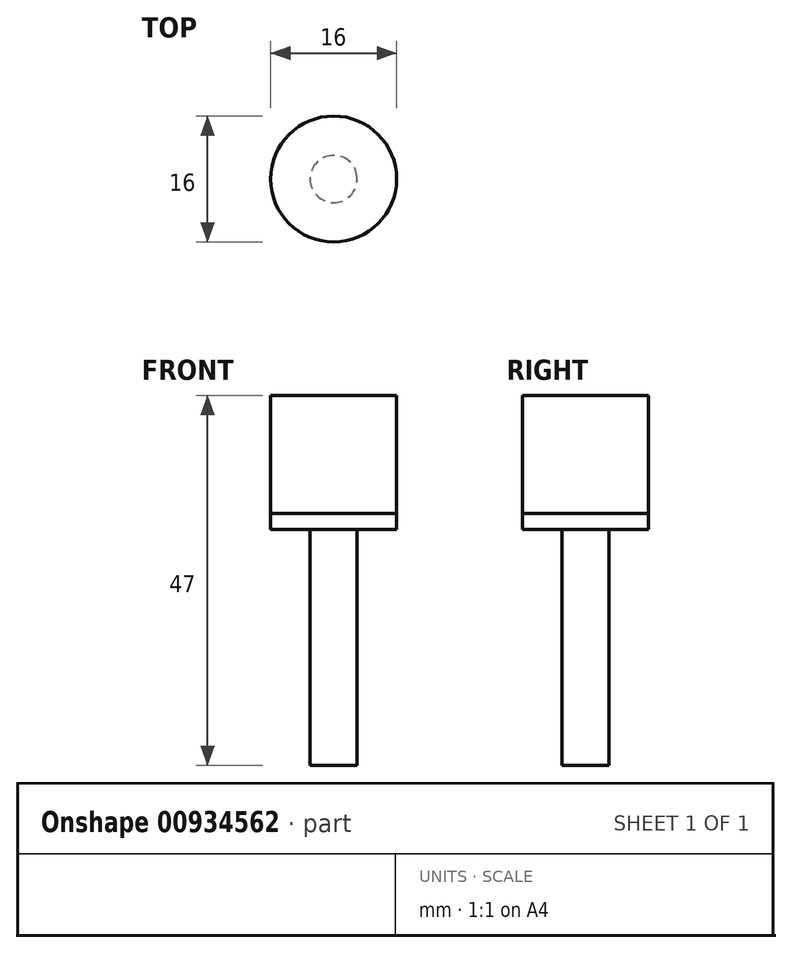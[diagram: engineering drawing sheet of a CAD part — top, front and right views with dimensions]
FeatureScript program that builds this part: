
annotation { "Feature Type Name" : "Feature", "Feature Type Description" : "" }
export const myFeature = defineFeature(function(context is Context, id is Id, definition is map)
    precondition{}
    {
        {
            var Q0;
            Q0=qCreatedBy(makeId("Front.planeOp"),FACE);
            var sketch = newSketch(context, id + "F0", { "sketchPlane" : qUnion([Q0])});
            skLineSegment(sketch, "E0", {"start": v(0, 0) * mm, "end": v(-3, 0) * mm});
            skLineSegment(sketch, "E1", {"start": v(-3, 0) * mm, "end": v(-3, 30) * mm});
            skLineSegment(sketch, "E2", {"start": v(-3, 30) * mm, "end": v(-8, 30) * mm});
            skLineSegment(sketch, "E3", {"start": v(-8, 30) * mm, "end": v(-8, 32) * mm});
            skLineSegment(sketch, "E4", {"start": v(-8, 32) * mm, "end": v(0, 32) * mm});
            skLineSegment(sketch, "E5", {"start": v(0, 32) * mm, "end": v(0, 0) * mm});
            skSolve(sketch);
        }
        {
            var Q0;
            Q0=makeQuery(id+"F0.imprint","IMPRINT",FACE,{"disambiguationData":[TD([[makeQuery(id+"F0.imprint","IMPRINT",EDGE,{"derivedFrom":sQuery(id+"F0.wireOp",EDGE,"E0")}),-1.0]])]});
            var Q1;
            Q1=sQuery(id+"F0.wireOp",EDGE,"E5");
            revolve(context, id + "F1", {"surfaceOperationType" : NewSurfaceOperationType.NEW, "entities" : qUnion([Q0]), "axis" : qUnion([Q1]), "revolveType" : RevolveType.FULL});
        }
        {
            var Q0;
            Q0=makeQuery(id+"F1.opRevolve","SWEPT_FACE",FACE,{"disambiguationData":[OSD([sQuery(id+"F0.wireOp",EDGE,"E4")])]});
            extrude(context, id + "F2", {"entities" : qUnion([Q0]), "depth" : 15 * mm, "offsetDistance" : 25 * mm});
        }
    });
